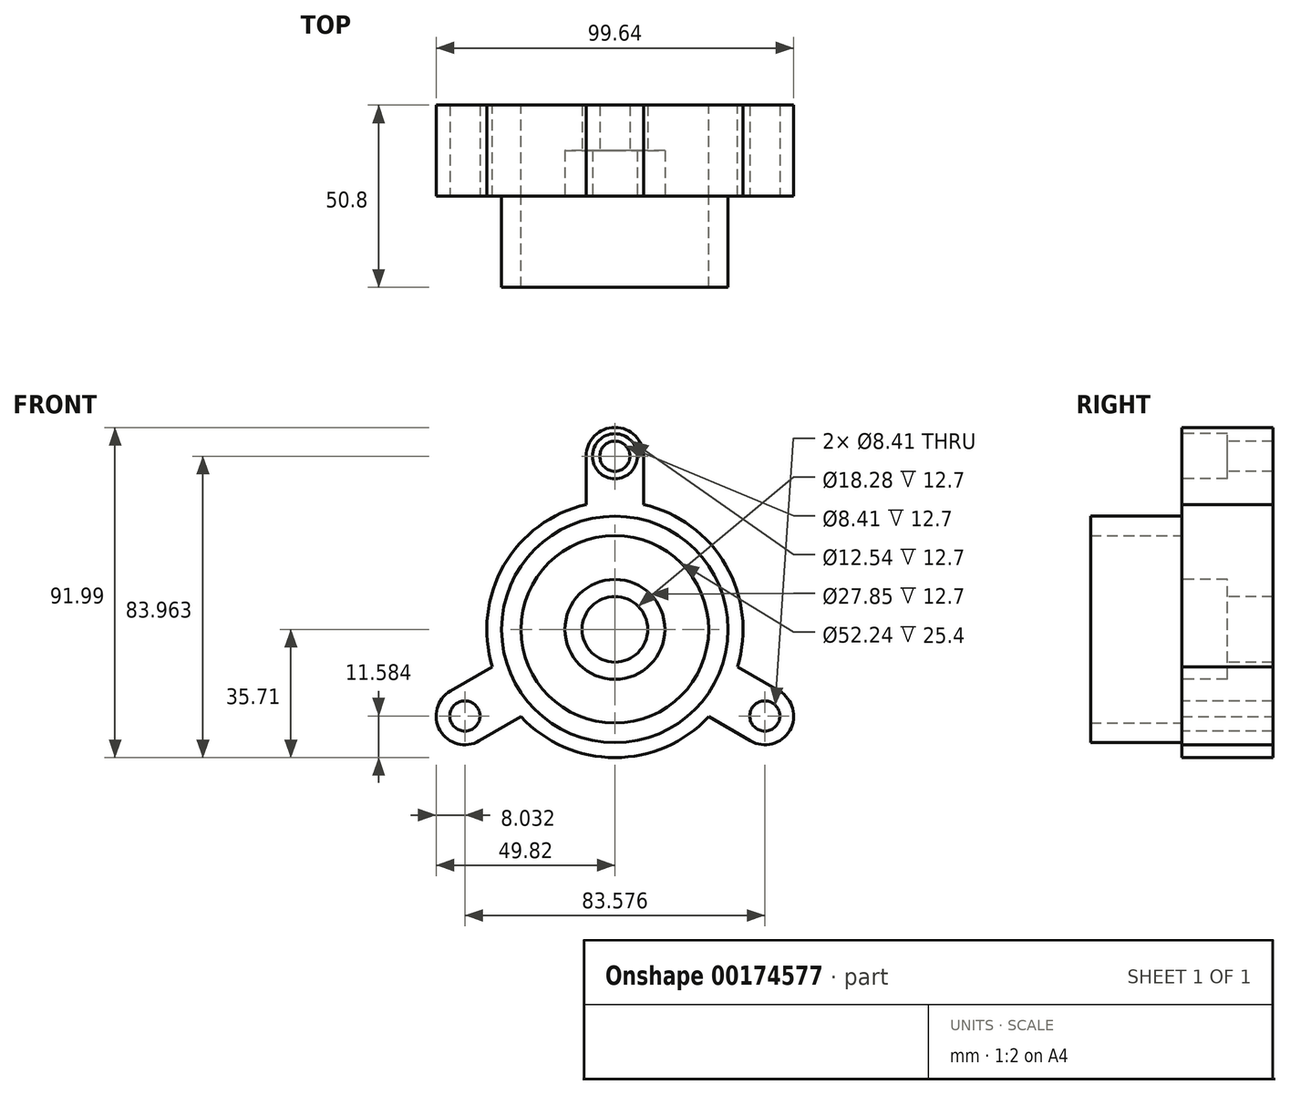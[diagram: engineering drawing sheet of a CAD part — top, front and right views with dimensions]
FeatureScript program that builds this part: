
annotation { "Feature Type Name" : "Feature", "Feature Type Description" : "" }
export const myFeature = defineFeature(function(context is Context, id is Id, definition is map)
    precondition{}
    {
        {
            var Q0;
            Q0=qCreatedBy(makeId("Front.planeOp"),FACE);
            var sketch = newSketch(context, id + "F0", { "sketchPlane" : qUnion([Q0])});
            skArc(sketch, "E0", {"start": v(-8.03, 34.8) * mm, "mid": v(0, -35.71) * mm, "end": v(8.03, 34.8) * mm});
            skLineSegment(sketch, "E1.left", {"start": v(-8.03, 48.25) * mm, "end": v(-8.03, 34.8) * mm});
            skLineSegment(sketch, "E1.right", {"start": v(8.03, 48.25) * mm, "end": v(8.03, 34.8) * mm});
            skPoint(sketch, "E1.middle", {"position": v(0, 35.71) * mm});
            skArc(sketch, "E2", {"start": v(8.03, 48.25) * mm, "mid": v(0, 56.28) * mm, "end": v(-8.03, 48.25) * mm});
            skPoint(sketch, "E3.orphan", {"position": v(-8.03, 23.17) * mm});
            skPoint(sketch, "E4.orphan", {"position": v(8.03, 23.17) * mm});
            skLineSegment(sketch, "E5.1.0", {"start": v(-37.77, -31.08) * mm, "end": v(-26.12, -24.35) * mm});
            skLineSegment(sketch, "E5.1.1", {"start": v(-45.8, -17.17) * mm, "end": v(-34.15, -10.45) * mm});
            skArc(sketch, "E5.1.2", {"start": v(-45.8, -17.17) * mm, "mid": v(-48.74, -28.14) * mm, "end": v(-37.77, -31.08) * mm});
            skLineSegment(sketch, "E5.2.0", {"start": v(45.8, -17.17) * mm, "end": v(34.15, -10.45) * mm});
            skLineSegment(sketch, "E5.2.1", {"start": v(37.77, -31.08) * mm, "end": v(26.12, -24.35) * mm});
            skArc(sketch, "E5.2.2", {"start": v(37.77, -31.08) * mm, "mid": v(48.74, -28.14) * mm, "end": v(45.8, -17.17) * mm});
            skSolve(sketch);
        }
        {
            var Q0;
            Q0 = qSketchRegion(id + "F0", true);
            extrude(context, id + "F1", {"entities" : qUnion([Q0]), "depth" : 25.4 * mm});
        }
        {
            var Q0;
            Q0=makeQuery(id+"F1.opExtrude","CAP_FACE",FACE,{"disambiguationData":[OSD([sQuery(id+"F0.wireOp",EDGE,"E0"),sQuery(id+"F0.wireOp",EDGE,"E1.left"),sQuery(id+"F0.wireOp",EDGE,"E1.right"),sQuery(id+"F0.wireOp",EDGE,"E2"),sQuery(id+"F0.wireOp",EDGE,"E5.1.0"),sQuery(id+"F0.wireOp",EDGE,"E5.1.1"),sQuery(id+"F0.wireOp",EDGE,"E5.1.2"),sQuery(id+"F0.wireOp",EDGE,"E5.2.0"),sQuery(id+"F0.wireOp",EDGE,"E5.2.1"),sQuery(id+"F0.wireOp",EDGE,"E5.2.2")])],"isStart":false});
            var sketch = newSketch(context, id + "F2", { "sketchPlane" : qUnion([Q0])});
            skCircle(sketch, "E6", {"center": v(0, 48.25) * mm, "radius": 4.2 * mm});
            skCircle(sketch, "E7.1.0", {"center": v(-41.79, -24.13) * mm, "radius": 4.2 * mm});
            skCircle(sketch, "E7.2.0", {"center": v(41.79, -24.13) * mm, "radius": 4.2 * mm});
            skPoint(sketch, "E7.center", {"position": v(0, 0) * mm});
            skSolve(sketch);
        }
        {
            var Q0;
            Q0=makeQuery(id+"F2.imprint","IMPRINT",FACE,{"disambiguationData":[TD([[makeQuery(id+"F2.imprint","IMPRINT",EDGE,{"derivedFrom":sQuery(id+"F2.wireOp",EDGE,"E6")}),1.0]])]});
            var Q1;
            Q1=makeQuery(id+"F2.imprint","IMPRINT",FACE,{"disambiguationData":[TD([[makeQuery(id+"F2.imprint","IMPRINT",EDGE,{"derivedFrom":sQuery(id+"F2.wireOp",EDGE,"E7.1.0")}),1.0]])]});
            var Q2;
            Q2=makeQuery(id+"F2.imprint","IMPRINT",FACE,{"disambiguationData":[TD([[makeQuery(id+"F2.imprint","IMPRINT",EDGE,{"derivedFrom":sQuery(id+"F2.wireOp",EDGE,"E7.2.0")}),1.0]])]});
            extrude(context, id + "F3", {"entities" : qUnion([Q0, Q1, Q2]), "operationType" : NewBodyOperationType.REMOVE, "endBound" : BoundingType.THROUGH_ALL, "oppositeDirection" : true, "depth" : 25.4 * mm});
        }
        {
            var Q0;
            Q0=makeQuery(id+"F1.opExtrude","CAP_FACE",FACE,{"disambiguationData":[OSD([sQuery(id+"F0.wireOp",EDGE,"E0"),sQuery(id+"F0.wireOp",EDGE,"E1.left"),sQuery(id+"F0.wireOp",EDGE,"E1.right"),sQuery(id+"F0.wireOp",EDGE,"E2"),sQuery(id+"F0.wireOp",EDGE,"E5.1.0"),sQuery(id+"F0.wireOp",EDGE,"E5.1.1"),sQuery(id+"F0.wireOp",EDGE,"E5.1.2"),sQuery(id+"F0.wireOp",EDGE,"E5.2.0"),sQuery(id+"F0.wireOp",EDGE,"E5.2.1"),sQuery(id+"F0.wireOp",EDGE,"E5.2.2")])],"isStart":false});
            var sketch = newSketch(context, id + "F4", { "sketchPlane" : qUnion([Q0])});
            skCircle(sketch, "E8", {"center": v(0, 48.25) * mm, "radius": 6.27 * mm});
            skCircle(sketch, "E9.1.0", {"center": v(-41.79, -24.13) * mm, "radius": 6.27 * mm});
            skCircle(sketch, "E9.2.0", {"center": v(41.79, -24.13) * mm, "radius": 6.27 * mm});
            skPoint(sketch, "E9.center", {"position": v(0, 0) * mm});
            skSolve(sketch);
        }
        {
            var Q0;
            Q0=makeQuery(id+"F4.imprint","IMPRINT",FACE,{"disambiguationData":[TD([[makeQuery(id+"F4.imprint","IMPRINT",EDGE,{"derivedFrom":sQuery(id+"F4.wireOp",EDGE,"E8")}),-1.0]])]});
            var sketch = newSketch(context, id + "F5", { "sketchPlane" : qUnion([Q0])});
            skSolve(sketch);
        }
        {
            var Q0;
            Q0=makeQuery(id+"F4.imprint","IMPRINT",FACE,{"disambiguationData":[TD([[makeQuery(id+"F4.imprint","IMPRINT",EDGE,{"derivedFrom":sQuery(id+"F4.wireOp",EDGE,"E8")}),1.0]])]});
            var Q1;
            Q1=sQuery(id+"F4.wireOp",EDGE,"E8");
            extrude(context, id + "F6", {"entities" : qUnion([Q0]), "operationType" : NewBodyOperationType.REMOVE, "surfaceEntities" : qUnion([Q1]), "oppositeDirection" : true, "depth" : 12.7 * mm});
        }
        {
            var Q0;
            Q0=makeQuery(id+"F5.imprint","IMPRINT",FACE,{"disambiguationData":[TD([[makeQuery(id+"F5.imprint","IMPRINT",EDGE,{"derivedFrom":makeQuery(id+"F4.imprint","IMPRINT",EDGE,{"derivedFrom":sQuery(id+"F4.wireOp",EDGE,"E8")})}),-1.0]])]});
            var sketch = newSketch(context, id + "F7", { "sketchPlane" : qUnion([Q0])});
            skCircle(sketch, "E10", {"center": v(0, 0) * mm, "radius": 9.14 * mm});
            skSolve(sketch);
        }
        {
            var Q0;
            Q0 = qSketchRegion(id + "F7", true);
            extrude(context, id + "F8", {"entities" : qUnion([Q0]), "operationType" : NewBodyOperationType.REMOVE, "endBound" : BoundingType.THROUGH_ALL, "oppositeDirection" : true, "depth" : 25.4 * mm});
        }
        {
            var Q0;
            Q0=makeQuery(id+"F5.imprint","IMPRINT",FACE,{"disambiguationData":[TD([[makeQuery(id+"F5.imprint","IMPRINT",EDGE,{"derivedFrom":makeQuery(id+"F4.imprint","IMPRINT",EDGE,{"derivedFrom":sQuery(id+"F4.wireOp",EDGE,"E8")})}),-1.0]])]});
            var sketch = newSketch(context, id + "F9", { "sketchPlane" : qUnion([Q0])});
            skCircle(sketch, "E11", {"center": v(0, 0) * mm, "radius": 13.93 * mm});
            skSolve(sketch);
        }
        {
            var Q0;
            Q0 = qSketchRegion(id + "F9", true);
            extrude(context, id + "F10", {"entities" : qUnion([Q0]), "operationType" : NewBodyOperationType.REMOVE, "oppositeDirection" : true, "depth" : 12.7 * mm});
        }
        {
            var Q0;
            Q0=makeQuery(id+"F5.imprint","IMPRINT",FACE,{"disambiguationData":[TD([[makeQuery(id+"F5.imprint","IMPRINT",EDGE,{"derivedFrom":makeQuery(id+"F4.imprint","IMPRINT",EDGE,{"derivedFrom":sQuery(id+"F4.wireOp",EDGE,"E8")})}),-1.0]])]});
            var sketch = newSketch(context, id + "F11", { "sketchPlane" : qUnion([Q0])});
            skCircle(sketch, "E12", {"center": v(0, 0) * mm, "radius": 31.56 * mm});
            skCircle(sketch, "E13", {"center": v(0, 0) * mm, "radius": 26.12 * mm});
            skSolve(sketch);
        }
        {
            var Q0;
            Q0 = qSketchRegion(id + "F11", true);
            extrude(context, id + "F12", {"entities" : qUnion([Q0]), "operationType" : NewBodyOperationType.ADD, "depth" : 25.4 * mm});
        }
    });
